# Revit family: QF_ELECTROLUXPROFESSIONAL_CC0HN7_CC0HN7
name_source: partatom
category: Specialty Equipment
units: mm (PartAtom-declared; Revit-internal decimal feet)

## family parameters
Always vertical = Yes
Cut with Voids When Loaded = No
Enable Cutting in Views = No
Maintain Annotation Orientation = No
Part Type = Normal
Room Calculation Point = No
Round Connector Dimension = Use Diameter
Shared = No
Work Plane-Based = No

## types (1)
- Standard
    Accessory = Yes
    Cold Water Size = 0 mm
    Compressed Air Pressure = 0.0 Pa
    Compressed Air Size = 0 mm
    Compressed Air Volume = 0.0 L/s
    Condensate Return Size = 0 mm
    Cycle = 60 Hz
    Default Elevation = 0 mm  [stored 0 ft]
    Depth Actual = 1180 mm
    Description = BAIN-MARIE, WATER, SINGLE WELL, 2GN+WHEELS H=900MM OVERSHELF WITH HOT LIGHTS
    Direct Waste Size = 19 mm
    Gas Input Pressure = 0
    Gas KW = 0
    Gas Size = 0 mm
    HP = 0 HP
    Height Actual = 1304 mm
    Hot Water Size = 0 mm
    Item Number = CC0HN7
    Length Actual = 770 mm
    Manufacturer = Electrolux Professional
    Model = CC0HN7
    Phase = 1
    Refrigerant Compressor Remote = Yes
    Refrigeration Liquid Line Size = 0 mm
    Refrigeration Suction Line Size = 0 mm
    Steam Pounds per Hour = 0
    Steam Supply Maximum Pressure = 0.0 Pa
    Steam Supply Minimum Pressure = 0.0 Pa
    Steam Supply Size = 0 mm
    URL = http://professional.electrolux.com
    URL Manufacturer = http://professional.electrolux.com
    Volts = 220 V
    Watts = 0 W
    Weight = 94.50 kg

note: source unit labels omitted for Gas Input Pressure — the stored unit's dimension contradicts the parameter name (converter mislabeling)

note: [stored X ft] marks values corroborated as IEEE doubles in the binary element streams (Revit-internal decimal feet)

## geometry (parser evidence)
native form markers: Blend x8, Sweep x5
no freeform markers — native parametric forms only
